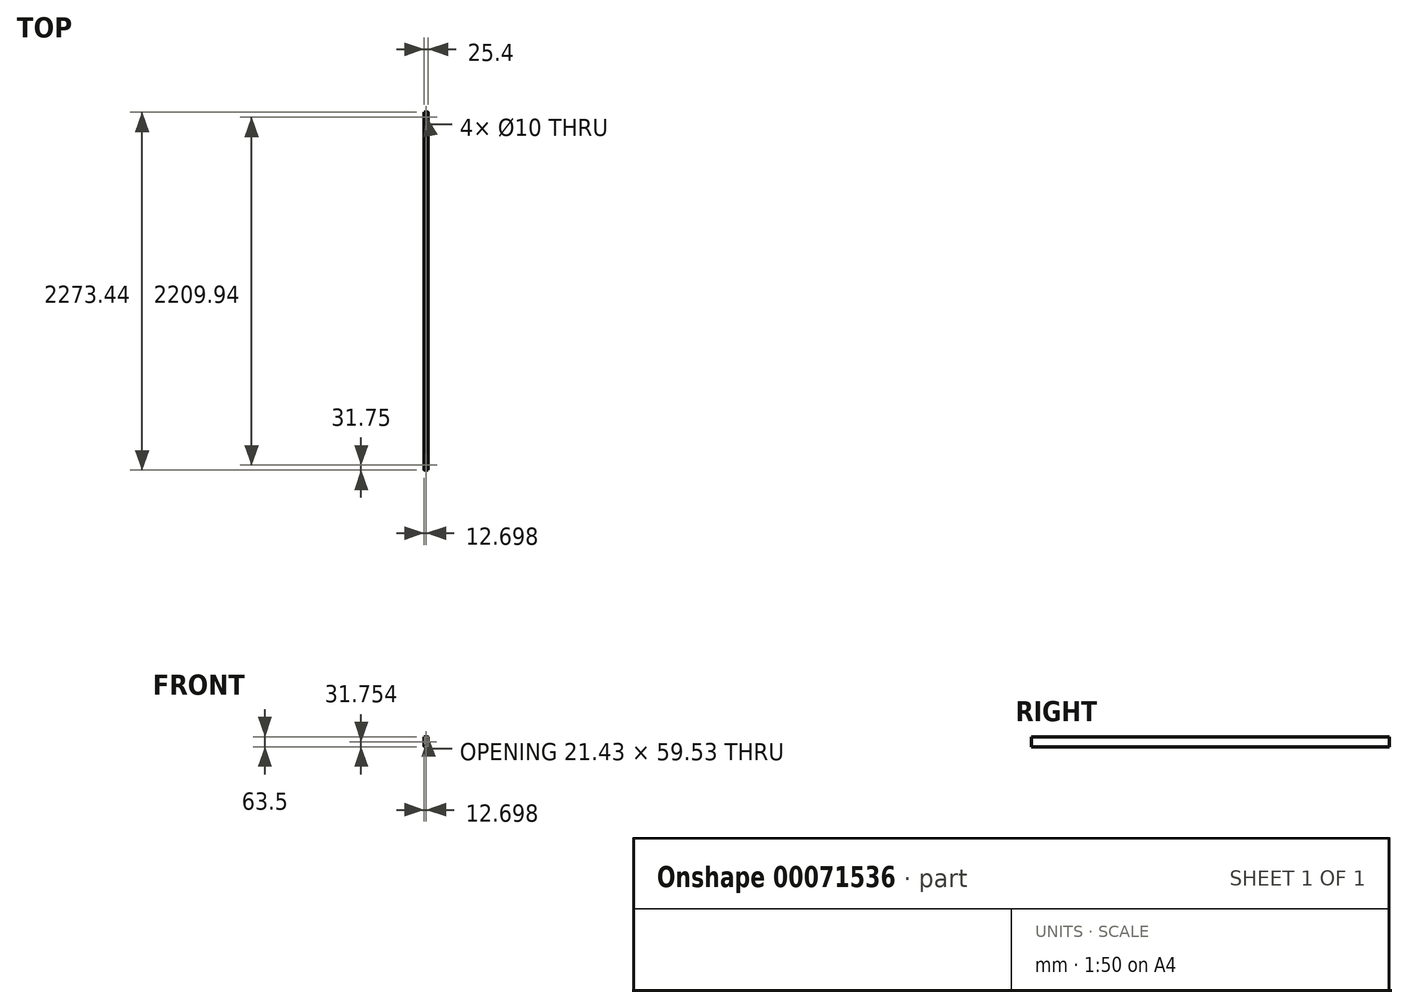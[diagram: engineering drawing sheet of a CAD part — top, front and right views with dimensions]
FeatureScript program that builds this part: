
annotation { "Feature Type Name" : "Feature", "Feature Type Description" : "" }
export const myFeature = defineFeature(function(context is Context, id is Id, definition is map)
    precondition{}
    {
        {
            var Q0;
            Q0=qCreatedBy(makeId("Front.planeOp"),FACE);
            var sketch = newSketch(context, id + "F0", { "sketchPlane" : qUnion([Q0])});
            skLineSegment(sketch, "E0.bottom", {"start": v(-2.93, 41.96) * mm, "end": v(16.47, 41.96) * mm});
            skLineSegment(sketch, "E0.top", {"start": v(-2.93, -21.54) * mm, "end": v(16.47, -21.54) * mm});
            skLineSegment(sketch, "E0.left", {"start": v(-5.93, 38.96) * mm, "end": v(-5.93, -18.54) * mm});
            skLineSegment(sketch, "E0.right", {"start": v(19.47, 38.96) * mm, "end": v(19.47, -18.54) * mm});
            skLineSegment(sketch, "E1.bottom", {"start": v(-0.95, 39.98) * mm, "end": v(14.48, 39.98) * mm});
            skLineSegment(sketch, "E1.top", {"start": v(-0.95, -19.55) * mm, "end": v(14.48, -19.55) * mm});
            skLineSegment(sketch, "E1.left", {"start": v(-3.95, 36.98) * mm, "end": v(-3.95, -16.55) * mm});
            skLineSegment(sketch, "E1.right", {"start": v(17.48, 36.98) * mm, "end": v(17.48, -16.55) * mm});
            skPoint(sketch, "E2.visualSharp", {"position": v(-3.95, 39.98) * mm});
            skArc(sketch, "E2.filletArc", {"start": v(-0.95, 39.98) * mm, "mid": v(-3.07, 39.1) * mm, "end": v(-3.95, 36.98) * mm});
            skPoint(sketch, "E3.visualSharp", {"position": v(17.48, 39.98) * mm});
            skArc(sketch, "E3.filletArc", {"start": v(17.48, 36.98) * mm, "mid": v(16.6, 39.1) * mm, "end": v(14.48, 39.98) * mm});
            skPoint(sketch, "E4.visualSharp", {"position": v(17.48, -19.55) * mm});
            skArc(sketch, "E4.filletArc", {"start": v(14.48, -19.55) * mm, "mid": v(16.6, -18.67) * mm, "end": v(17.48, -16.55) * mm});
            skPoint(sketch, "E5.visualSharp", {"position": v(-3.95, -19.55) * mm});
            skArc(sketch, "E5.filletArc", {"start": v(-3.95, -16.55) * mm, "mid": v(-3.07, -18.67) * mm, "end": v(-0.95, -19.55) * mm});
            skPoint(sketch, "E6.visualSharp", {"position": v(19.47, -21.54) * mm});
            skArc(sketch, "E6.filletArc", {"start": v(16.47, -21.54) * mm, "mid": v(18.59, -20.66) * mm, "end": v(19.47, -18.54) * mm});
            skPoint(sketch, "E7.visualSharp", {"position": v(19.47, 41.96) * mm});
            skArc(sketch, "E7.filletArc", {"start": v(19.47, 38.96) * mm, "mid": v(18.59, 41.09) * mm, "end": v(16.47, 41.96) * mm});
            skPoint(sketch, "E8.visualSharp", {"position": v(-5.93, 41.96) * mm});
            skArc(sketch, "E8.filletArc", {"start": v(-2.93, 41.96) * mm, "mid": v(-5.05, 41.09) * mm, "end": v(-5.93, 38.96) * mm});
            skPoint(sketch, "E9.visualSharp", {"position": v(-5.93, -21.54) * mm});
            skArc(sketch, "E9.filletArc", {"start": v(-5.93, -18.54) * mm, "mid": v(-5.05, -20.66) * mm, "end": v(-2.93, -21.54) * mm});
            skSolve(sketch);
        }
        {
            var Q0;
            Q0 = qSketchRegion(id + "F0", true);
            extrude(context, id + "F1", {"entities" : qUnion([Q0]), "depth" : 2273.44 * mm});
        }
        {
            var Q0;
            Q0=makeQuery(id+"F1.opExtrude","SWEPT_FACE",FACE,{"disambiguationData":[OSD([sQuery(id+"F0.wireOp",EDGE,"E0.bottom")])]});
            var sketch = newSketch(context, id + "F2", { "sketchPlane" : qUnion([Q0])});
            skCircle(sketch, "E10", {"center": v(6.77, -2241.69) * mm, "radius": 5 * mm});
            skCircle(sketch, "E11", {"center": v(6.77, -31.75) * mm, "radius": 5 * mm});
            skSolve(sketch);
        }
        {
            var Q0;
            Q0 = qSketchRegion(id + "F2", true);
            extrude(context, id + "F3", {"entities" : qUnion([Q0]), "operationType" : NewBodyOperationType.REMOVE, "endBound" : BoundingType.THROUGH_ALL, "oppositeDirection" : true, "depth" : 25 * mm});
        }
    });
